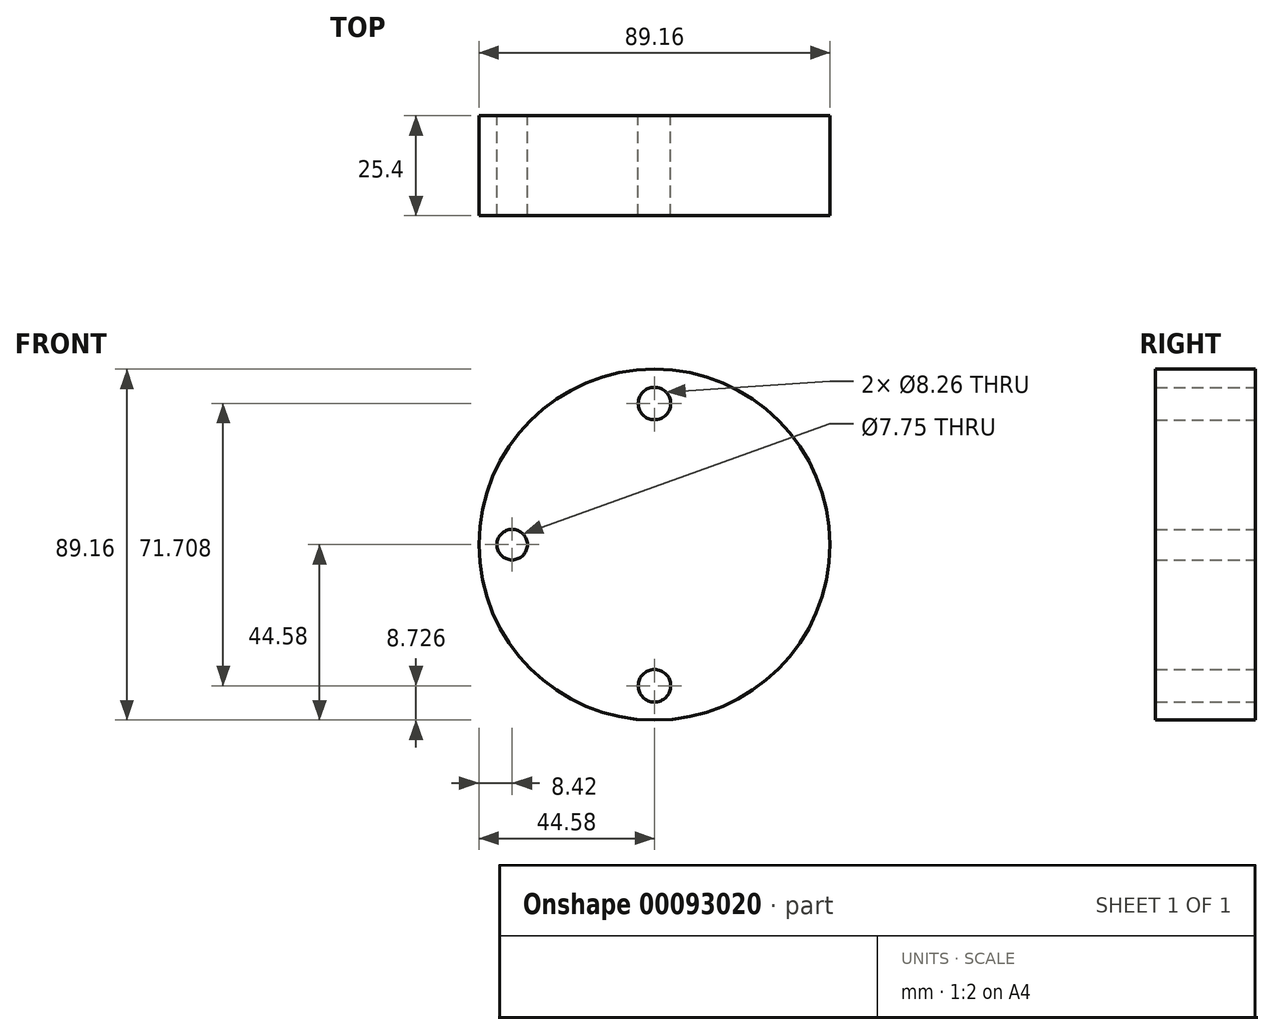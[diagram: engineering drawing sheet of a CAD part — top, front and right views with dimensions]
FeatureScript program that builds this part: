
annotation { "Feature Type Name" : "Feature", "Feature Type Description" : "" }
export const myFeature = defineFeature(function(context is Context, id is Id, definition is map)
    precondition{}
    {
        {
            var Q0;
            Q0=qCreatedBy(makeId("Front.planeOp"),FACE);
            var sketch = newSketch(context, id + "F0", { "sketchPlane" : qUnion([Q0])});
            skCircle(sketch, "E0", {"center": v(0, 0) * mm, "radius": 44.58 * mm});
            skCircle(sketch, "E1", {"center": v(0, 35.85) * mm, "radius": 4.13 * mm});
            skCircle(sketch, "E2", {"center": v(-36.16, 0) * mm, "radius": 3.87 * mm});
            skCircle(sketch, "E3.MirrorC", {"center": v(0, -35.85) * mm, "radius": 4.13 * mm});
            skSolve(sketch);
        }
        {
            var Q0;
            Q0=makeQuery(id+"F0.imprint","IMPRINT",FACE,{"disambiguationData":[TD([[makeQuery(id+"F0.imprint","IMPRINT",EDGE,{"derivedFrom":sQuery(id+"F0.wireOp",EDGE,"E0")}),1.0]])]});
            extrude(context, id + "F1", {"entities" : qUnion([Q0]), "depth" : 25.4 * mm});
        }
    });
